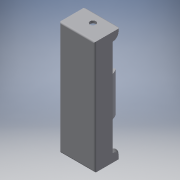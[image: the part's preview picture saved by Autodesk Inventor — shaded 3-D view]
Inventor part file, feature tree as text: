
AUTODESK INVENTOR PART (.ipt)
format: ipt  version: 2016 (Build 200138000, 138)  size: 214,016 bytes
history: native  units: mm
features: extrude x8, sketch x8, fillet x2, chamfer x1
ambient origin geometry x8: Origin, YZ Plane, XZ Plane, XY Plane, X Axis, Y Axis, Z Axis, Center Point
bodies: Solid1 (feature_tree)
feature tree (19):
  extrude  "Extrusion1"  Depth=57.5mm
  extrude  "Extrusion2"  Depth=1.25mm
  extrude  "Extrusion3"  Depth=1.25mm
  extrude  "Extrusion4"  Depth=1.25mm
  extrude  "Extrusion5"  Depth=6.0mm TaperAngle=0.0deg
  extrude  "Extrusion6"  Depth=1.25mm TaperAngle=0.0deg
  extrude  "Extrusion7"  Depth=20.0mm TaperAngle=0.0deg
  extrude  "Extrusion8"  Depth=20.0mm TaperAngle=0.0deg
  chamfer  "Chamfer2"  Distance=1.0mm Angle=45.0deg
  fillet  "Fillet1"  Radius=0.75mm
  fillet  "Fillet2"  Radius=0.75mm
  sketch  "Sketch1"  dims[d0=18.0mm d1=57.5mm]
  sketch  "Sketch2"  dims[d2=3.0mm d3=0.0mm d4=1.25mm]
  sketch  "Sketch3"  dims[d5=18.0mm d6=1.25mm]
  sketch  "Sketch4"  dims[d7=10.0mm d8=0.0mm d9=1.25mm]
  sketch  "Sketch5"  dims[d10=1.25mm d11=6.0mm d12=0.0mm]
  sketch  "Sketch6"  dims[d13=1.25mm d14=0.0mm d15=1.25mm d16=0.0mm]
  sketch  "Sketch7"  dims[d20=20.0mm d21=0.0mm d22=20.0mm d23=0.0mm]
  sketch  "Sketch8"  dims[d24=5.0mm d26=20.0mm d27=0.0mm d31=1.0mm d32=2.0mm d33=45.0deg d34=0.75mm d35=0.75mm d36=3.0mm]
